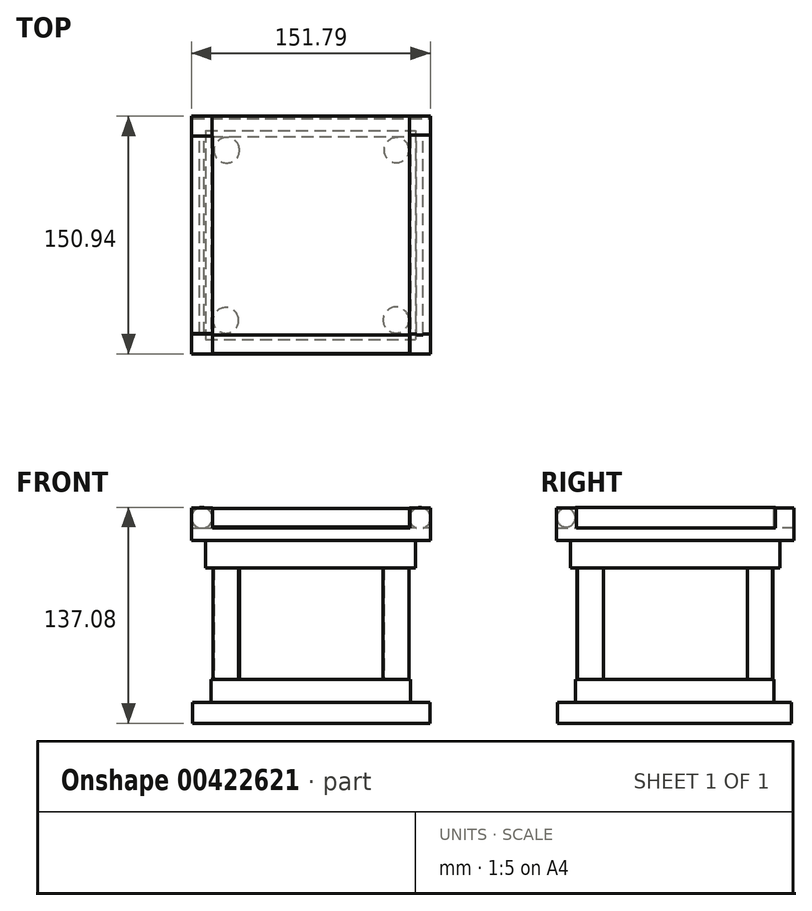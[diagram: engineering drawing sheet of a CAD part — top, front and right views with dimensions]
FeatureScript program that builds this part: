
annotation { "Feature Type Name" : "Feature", "Feature Type Description" : "" }
export const myFeature = defineFeature(function(context is Context, id is Id, definition is map)
    precondition{}
    {
        {
            var Q0;
            Q0=qCreatedBy(makeId("Top.planeOp"),FACE);
            var sketch = newSketch(context, id + "F0", { "sketchPlane" : qUnion([Q0])});
            skLineSegment(sketch, "E0.bottom", {"start": v(-75.5, -74.04) * mm, "end": v(75.06, -74.04) * mm});
            skLineSegment(sketch, "E0.top", {"start": v(-75.5, 74.8) * mm, "end": v(75.06, 74.8) * mm});
            skLineSegment(sketch, "E0.left", {"start": v(-75.5, -74.04) * mm, "end": v(-75.5, 74.8) * mm});
            skLineSegment(sketch, "E0.right", {"start": v(75.06, -74.04) * mm, "end": v(75.06, 74.8) * mm});
            skSolve(sketch);
        }
        {
            var Q0;
            Q0 = qSketchRegion(id + "F0", true);
            extrude(context, id + "F1", {"entities" : qUnion([Q0]), "oppositeDirection" : true, "depth" : 13.2 * mm});
        }
        {
            var Q0;
            Q0=makeQuery(id+"F1.opExtrude","CAP_FACE",FACE,{"disambiguationData":[OSD([sQuery(id+"F0.wireOp",EDGE,"E0.bottom"),sQuery(id+"F0.wireOp",EDGE,"E0.top"),sQuery(id+"F0.wireOp",EDGE,"E0.left"),sQuery(id+"F0.wireOp",EDGE,"E0.right")])],"isStart":true});
            var sketch = newSketch(context, id + "F2", { "sketchPlane" : qUnion([Q0])});
            skLineSegment(sketch, "E1.bottom", {"start": v(-63.84, 63.55) * mm, "end": v(62.7, 63.55) * mm});
            skLineSegment(sketch, "E1.top", {"start": v(-63.84, -62.42) * mm, "end": v(62.7, -62.42) * mm});
            skLineSegment(sketch, "E1.left", {"start": v(-63.84, 63.55) * mm, "end": v(-63.84, -62.42) * mm});
            skLineSegment(sketch, "E1.right", {"start": v(62.7, 63.55) * mm, "end": v(62.7, -62.42) * mm});
            skSolve(sketch);
        }
        {
            var Q0;
            Q0 = qSketchRegion(id + "F2", true);
            extrude(context, id + "F3", {"entities" : qUnion([Q0]), "operationType" : NewBodyOperationType.ADD, "depth" : 14.48 * mm});
        }
        {
            var Q0;
            Q0=makeQuery(id+"F3.opExtrude","CAP_FACE",FACE,{"disambiguationData":[OSD([sQuery(id+"F2.wireOp",EDGE,"E1.bottom"),sQuery(id+"F2.wireOp",EDGE,"E1.top"),sQuery(id+"F2.wireOp",EDGE,"E1.left"),sQuery(id+"F2.wireOp",EDGE,"E1.right")])],"isStart":false});
            var sketch = newSketch(context, id + "F4", { "sketchPlane" : qUnion([Q0])});
            skCircle(sketch, "E2", {"center": v(-53.9, 54.76) * mm, "radius": 8.11 * mm});
            skCircle(sketch, "E3", {"center": v(-54.47, -53.34) * mm, "radius": 8.17 * mm});
            skCircle(sketch, "E4", {"center": v(53.62, -53.06) * mm, "radius": 8.23 * mm});
            skCircle(sketch, "E5", {"center": v(53.9, 54.76) * mm, "radius": 7.95 * mm});
            skSolve(sketch);
        }
        {
            var Q0;
            Q0 = qSketchRegion(id + "F4", true);
            extrude(context, id + "F5", {"entities" : qUnion([Q0]), "operationType" : NewBodyOperationType.ADD, "depth" : 70.87 * mm});
        }
        {
            var Q0;
            Q0=makeQuery(id+"F5.opExtrude","CAP_FACE",FACE,{"disambiguationData":[OSD([sQuery(id+"F4.wireOp",EDGE,"E2")])],"isStart":false});
            var sketch = newSketch(context, id + "F6", { "sketchPlane" : qUnion([Q0])});
            skLineSegment(sketch, "E6.bottom", {"start": v(-67.24, 67.24) * mm, "end": v(66.1, 67.24) * mm});
            skLineSegment(sketch, "E6.top", {"start": v(-67.24, -65.54) * mm, "end": v(66.1, -65.54) * mm});
            skLineSegment(sketch, "E6.left", {"start": v(-67.24, 67.24) * mm, "end": v(-67.24, -65.54) * mm});
            skLineSegment(sketch, "E6.right", {"start": v(66.1, 67.24) * mm, "end": v(66.1, -65.54) * mm});
            skSolve(sketch);
        }
        {
            var Q0;
            Q0 = qSketchRegion(id + "F6", true);
            extrude(context, id + "F7", {"entities" : qUnion([Q0]), "operationType" : NewBodyOperationType.ADD, "depth" : 17.53 * mm});
        }
        {
            var Q0;
            Q0=makeQuery(id+"F7.opExtrude","CAP_FACE",FACE,{"disambiguationData":[OSD([sQuery(id+"F6.wireOp",EDGE,"E6.bottom"),sQuery(id+"F6.wireOp",EDGE,"E6.top"),sQuery(id+"F6.wireOp",EDGE,"E6.left"),sQuery(id+"F6.wireOp",EDGE,"E6.right")])],"isStart":false});
            var sketch = newSketch(context, id + "F8", { "sketchPlane" : qUnion([Q0])});
            skLineSegment(sketch, "E7.bottom", {"start": v(-76.32, 76.32) * mm, "end": v(75.47, 76.32) * mm});
            skLineSegment(sketch, "E7.top", {"start": v(-76.32, -74.62) * mm, "end": v(75.47, -74.62) * mm});
            skLineSegment(sketch, "E7.left", {"start": v(-76.32, 76.32) * mm, "end": v(-76.32, -74.62) * mm});
            skLineSegment(sketch, "E7.right", {"start": v(75.47, 76.32) * mm, "end": v(75.47, -74.62) * mm});
            skSolve(sketch);
        }
        {
            var Q0;
            Q0 = qSketchRegion(id + "F8", true);
            extrude(context, id + "F9", {"entities" : qUnion([Q0]), "operationType" : NewBodyOperationType.ADD, "depth" : 7.87 * mm});
        }
        {
            var Q0;
            Q0=makeQuery(id+"F9.opExtrude","CAP_FACE",FACE,{"disambiguationData":[OSD([sQuery(id+"F8.wireOp",EDGE,"E7.bottom"),sQuery(id+"F8.wireOp",EDGE,"E7.top"),sQuery(id+"F8.wireOp",EDGE,"E7.left"),sQuery(id+"F8.wireOp",EDGE,"E7.right")])],"isStart":false});
            var sketch = newSketch(context, id + "F10", { "sketchPlane" : qUnion([Q0])});
            skLineSegment(sketch, "E8.bottom", {"start": v(-76.32, 76.32) * mm, "end": v(-63.38, 76.32) * mm});
            skLineSegment(sketch, "E8.top", {"start": v(-76.32, 63.67) * mm, "end": v(-63.38, 63.67) * mm});
            skLineSegment(sketch, "E8.left", {"start": v(-76.32, 76.32) * mm, "end": v(-76.32, 63.67) * mm});
            skLineSegment(sketch, "E8.right", {"start": v(-63.38, 76.32) * mm, "end": v(-63.38, 63.67) * mm});
            skLineSegment(sketch, "E9.bottom", {"start": v(-76.32, -74.62) * mm, "end": v(-62.81, -74.62) * mm});
            skLineSegment(sketch, "E9.top", {"start": v(-76.32, -61.84) * mm, "end": v(-62.81, -61.84) * mm});
            skLineSegment(sketch, "E9.left", {"start": v(-76.32, -74.62) * mm, "end": v(-76.32, -61.84) * mm});
            skLineSegment(sketch, "E9.right", {"start": v(-62.81, -74.62) * mm, "end": v(-62.81, -61.84) * mm});
            skLineSegment(sketch, "E10.bottom", {"start": v(75.47, -74.62) * mm, "end": v(62.4, -74.62) * mm});
            skLineSegment(sketch, "E10.top", {"start": v(75.47, -61.84) * mm, "end": v(62.4, -61.84) * mm});
            skLineSegment(sketch, "E10.left", {"start": v(75.47, -74.62) * mm, "end": v(75.47, -61.84) * mm});
            skLineSegment(sketch, "E10.right", {"start": v(62.4, -74.62) * mm, "end": v(62.4, -61.84) * mm});
            skLineSegment(sketch, "E11.bottom", {"start": v(75.47, 76.32) * mm, "end": v(62.12, 76.32) * mm});
            skLineSegment(sketch, "E11.top", {"start": v(75.47, 64.52) * mm, "end": v(62.12, 64.52) * mm});
            skLineSegment(sketch, "E11.left", {"start": v(75.47, 76.32) * mm, "end": v(75.47, 64.52) * mm});
            skLineSegment(sketch, "E11.right", {"start": v(62.12, 76.32) * mm, "end": v(62.12, 64.52) * mm});
            skSolve(sketch);
        }
        {
            var Q0;
            Q0 = qSketchRegion(id + "F10", true);
            extrude(context, id + "F11", {"entities" : qUnion([Q0]), "operationType" : NewBodyOperationType.ADD, "depth" : 12.7 * mm});
        }
        {
            var Q0;
            Q0=makeQuery(id+"F11.opExtrude","SWEPT_FACE",FACE,{"disambiguationData":[OSD([sQuery(id+"F10.wireOp",EDGE,"E11.top")])]});
            var sketch = newSketch(context, id + "F12", { "sketchPlane" : qUnion([Q0])});
            skCircle(sketch, "E12", {"center": v(68.8, 117.1) * mm, "radius": 6.67 * mm});
            skPoint(sketch, "E12.centerSnap0", {"position": v(68.8, 110.74) * mm});
            skPoint(sketch, "E12.centerSnap1", {"position": v(62.12, 117.1) * mm});
            skSolve(sketch);
        }
        {
            var Q0;
            Q0 = qSketchRegion(id + "F12", true);
            extrude(context, id + "F13", {"entities" : qUnion([Q0]), "operationType" : NewBodyOperationType.ADD, "depth" : 127 * mm});
        }
        {
            var Q0;
            Q0=makeQuery(id+"F11.opExtrude","SWEPT_FACE",FACE,{"disambiguationData":[OSD([sQuery(id+"F10.wireOp",EDGE,"E8.top")])]});
            var sketch = newSketch(context, id + "F14", { "sketchPlane" : qUnion([Q0])});
            skCircle(sketch, "E13", {"center": v(-69.67, 117.22) * mm, "radius": 6.65 * mm});
            skSolve(sketch);
        }
        {
            var Q0;
            Q0 = qSketchRegion(id + "F14", true);
            extrude(context, id + "F15", {"entities" : qUnion([Q0]), "operationType" : NewBodyOperationType.ADD, "depth" : 125.48 * mm});
        }
        {
            var Q0;
            Q0=makeQuery(id+"F11.opExtrude","SWEPT_FACE",FACE,{"disambiguationData":[OSD([sQuery(id+"F10.wireOp",EDGE,"E9.right")])]});
            var sketch = newSketch(context, id + "F16", { "sketchPlane" : qUnion([Q0])});
            skCircle(sketch, "E14", {"center": v(-68.47, 117.32) * mm, "radius": 5.89 * mm});
            skSolve(sketch);
        }
        {
            var Q0;
            Q0 = qSketchRegion(id + "F16", true);
            extrude(context, id + "F17", {"entities" : qUnion([Q0]), "operationType" : NewBodyOperationType.ADD, "depth" : 124.97 * mm});
        }
    });
